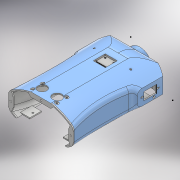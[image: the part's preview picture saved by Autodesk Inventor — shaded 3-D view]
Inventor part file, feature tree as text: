
AUTODESK INVENTOR PART (.ipt)
format: ipt  version: 2017 (Build 210142000, 142)  size: 1,997,824 bytes
history: native  units: mm
features: sketch x47, extrude x43, projected_geometry x24, plane x3, fillet x1, loft x1, mirror x1, shell x1, other x1
ambient origin geometry x8: Origin, YZ Plane, XZ Plane, XY Plane, X Axis, Y Axis, Z Axis, Center Point
bodies: Solid1 (feature_tree)
feature tree (122):
  extrude  "Extrusion1"  Depth=35.0mm
  extrude  "Extrusion2"  Depth=9.0mm TaperAngle=0.0deg
  extrude  "Extrusion6"  Depth=70.0mm TaperAngle=0.0deg
  extrude  "Extrusion9"  Depth=10.0mm
  extrude  "Extrusion11"  Depth=200.0mm
  fillet  "Fillet2"  [1 undecoded]
  sketch  "Sketch29"  dims[d72=0.0mm d73=90.0deg d81=2.0mm d83=-324.476mm]
  plane  "Work Plane8"
  loft  "Loft1"
  mirror  "Mirror8"
  shell  "Shell3"  Thickness=-324.476mm
  plane  "Work Plane9"
  extrude  "Extrusion16"  [1 undecoded]
  plane  "Work Plane10"
  extrude  "Extrusion17"  Depth=1.5mm TaperAngle=0.0deg
  extrude  "Extrusion18"  Depth=3.0mm TaperAngle=0.0deg
  extrude  "Extrusion19"  Depth=173.6141mm TaperAngle=0.0deg
  extrude  "Extrusion20"  Depth=200.0mm TaperAngle=0.0deg
  extrude  "Extrusion21"  Depth=6.0mm TaperAngle=0.0deg
  extrude  "Extrusion22"  Depth=6.0mm
  extrude  "Extrusion24"  Depth=6.0mm
  extrude  "Extrusion25"  Depth=1.5mm TaperAngle=0.0deg
  extrude  "Extrusion26"  Depth=150.0mm TaperAngle=0.0deg
  extrude  "Extrusion27"  Depth=20.0mm TaperAngle=0.0deg
  extrude  "Extrusion28"  Depth=2.0mm
  extrude  "Extrusion29"  Depth=2.0mm TaperAngle=0.0deg
  extrude  "Extrusion30"  Depth=1.0mm TaperAngle=0.0deg
  extrude  "Extrusion31"  Depth=5.0mm TaperAngle=0.0deg
  extrude  "Extrusion32"  Depth=1.0mm
  extrude  "Extrusion33"  Depth=23.0mm
  extrude  "Extrusion34"  Depth=3.0mm TaperAngle=0.0deg
  extrude  "Extrusion35"  Depth=6.8mm
  extrude  "Extrusion36"  Depth=6.8mm
  extrude  "Extrusion37"  Depth=120.0mm TaperAngle=0.0deg
  extrude  "Extrusion38"  Depth=43.0mm
  extrude  "Extrusion40"  Depth=41.0mm
  extrude  "Extrusion41"  Depth=4.0mm TaperAngle=0.0deg
  extrude  "Extrusion42"  Depth=8.1mm TaperAngle=0.0deg
  extrude  "Extrusion46"  Depth=10.0mm
  extrude  "Extrusion49"  Depth=3.0mm
  extrude  "Extrusion50"  Depth=8.0mm TaperAngle=0.0deg
  extrude  "Extrusion51"  Depth=150.0mm TaperAngle=0.0deg
  extrude  "Extrusion52"  Depth=3.0mm
  extrude  "Extrusion53"  TaperAngle=180.0deg  [1 undecoded]
  extrude  "Extrusion54"  Depth=10.0mm
  extrude  "Extrusion56"  Depth=5.0mm
  extrude  "Extrusion57"  Depth=3.0mm
  sketch  "Sketch89"
  extrude  "Extrusion58"  [1 undecoded]
  sketch  "Sketch91"
  sketch  "Sketch92"
  extrude  "Extrusion59"  [1 undecoded]
  extrude  "Extrusion60"  [1 undecoded]
  extrude  "Extrusion61"  [1 undecoded]
  sketch  "Sketch1"  dims[d0=63.0mm d1=0.0mm d2=35.0mm]
  sketch  "Sketch3"  dims[d3=150.0mm d4=9.0mm d5=0.0mm]
  sketch  "Sketch12"  dims[d30=250.0mm d31=0.0mm d48=70.0mm d49=0.0mm]
  sketch  "Sketch17"  dims[d53=70.0mm d54=0.0mm d55=10.0mm]
  sketch  "Sketch20"  dims[d68=-347.0mm d69=200.0mm d70=0.0mm d71=90.0deg]
  projected_geometry  "Projected Loop9"
  sketch  "Sketch30"  dims[d93=2.5mm d94=0.0mm d96=-15.524mm]
  other  "Edges1"
  sketch  "Sketch37"  dims[d102=4.0mm d103=0.0mm d104=1.5mm d105=0.0mm]
  sketch  "Sketch38"  dims[d106=2.0mm d107=0.0mm d111=3.0mm d112=0.0mm]
  sketch  "Sketch39"  dims[d113=12.0mm d114=0.0mm d115=173.6141mm d116=0.0mm]
  projected_geometry  "Projected Loop13"
  projected_geometry  "Projected Loop14"
  sketch  "Sketch41"  dims[d119=2.0mm d120=0.0mm d121=200.0mm d122=0.0mm]
  sketch  "Sketch43"  dims[d123=2.0mm d124=0.0mm d125=6.0mm d126=0.0mm]
  sketch  "Sketch44"  dims[d127=6.0mm d128=6.0mm]
  projected_geometry  "Projected Loop15"
  projected_geometry  "Projected Loop16"
  sketch  "Sketch46"  dims[d129=6.0mm d130=6.0mm]
  sketch  "Sketch50"  dims[d131=3.69mm d132=0.0mm d133=1.5mm d134=0.0mm]
  sketch  "Sketch51"  dims[d135=6.0mm d136=150.0mm d137=0.0mm]
  sketch  "Sketch52"  dims[d138=4.0mm d139=0.0mm d140=20.0mm d141=0.0mm]
  sketch  "Sketch53"  dims[d142=6.0mm d143=0.0mm d144=2.0mm]
  projected_geometry  "Projected Loop17"
  sketch  "Sketch55"  dims[d146=3.0mm d147=0.0mm d148=2.0mm d149=0.0mm]
  sketch  "Sketch56"  dims[d150=1.0mm d151=0.0mm d152=1.0mm d153=0.0mm]
  projected_geometry  "Projected Loop18"
  projected_geometry  "Projected Loop19"
  projected_geometry  "Projected Loop20"
  sketch  "Sketch57"  dims[d154=2.0mm d155=5.0mm d156=0.0mm]
  sketch  "Sketch58"  dims[d161=20.0mm d162=0.0mm d163=1.0mm]
  projected_geometry  "Projected Loop21"
  projected_geometry  "Projected Loop22"
  sketch  "Sketch59"  dims[d164=1.0mm d165=23.0mm]
  sketch  "Sketch61"  dims[d166=4.0mm d167=0.0mm d168=3.0mm d169=0.0mm]
  sketch  "Sketch62"  dims[d177=6.8mm d178=6.8mm]
  projected_geometry  "Projected Loop24"
  sketch  "Sketch63"  dims[d179=50.0mm d180=0.0mm d185=6.8mm]
  projected_geometry  "Projected Loop25"
  sketch  "Sketch64"  dims[d186=6.8mm d187=120.0mm d188=0.0mm]
  projected_geometry  "Projected Loop26"
  sketch  "Sketch65"  dims[d192=5.0mm d193=0.0mm d194=43.0mm]
  projected_geometry  "Projected Loop27"
  sketch  "Sketch66"  dims[d195=4.0mm d196=0.0mm d197=41.0mm]
  sketch  "Sketch68"  dims[d198=4.0mm d199=0.0mm d200=4.0mm d201=0.0mm]
  sketch  "Sketch69"  dims[d202=40.0mm d203=0.0mm d208=8.1mm d209=0.0mm]
  sketch  "Sketch70"  dims[d210=3.0mm d211=10.0mm]
  sketch  "Sketch74"  dims[d212=20.0mm d213=3.0mm]
  sketch  "Sketch77"  dims[d214=8.0mm d215=0.0mm d216=180.0mm d217=0.0mm]
  sketch  "Sketch78"  dims[d218=4.0mm d219=150.0mm d220=0.0mm]
  sketch  "Sketch81"  dims[d221=3.0mm d222=3.0mm]
  sketch  "Sketch82"  dims[d223=150.0mm d224=0.0mm d225=180.0deg]
  sketch  "Sketch83"  dims[d226=10.0mm d227=10.0mm]
  projected_geometry  "Projected Loop30"
  sketch  "Sketch84"  dims[d230=5.0mm d231=5.0mm]
  sketch  "Sketch87"  dims[d232=3.0mm d233=3.0mm]
  projected_geometry  "Projected Loop31"
  sketch  "Sketch88"  dims[d234=150.0mm d235=0.0mm]
  projected_geometry  "Projected Loop32"
  sketch  "Sketch90"
  projected_geometry  "Projected Loop33"
  projected_geometry  "Projected Loop34"
  projected_geometry  "Projected Loop40"
  projected_geometry  "Projected Loop41"
  projected_geometry  "Projected Loop42"
  projected_geometry  "Projected Loop43"
  sketch  "Sketch95"
  sketch  "Sketch96"
note: 7 required parameter values undecoded (feature->parameter linkage not recoverable at this tier; creation-order binding heuristic only, values carry confidence <= 0.55)
